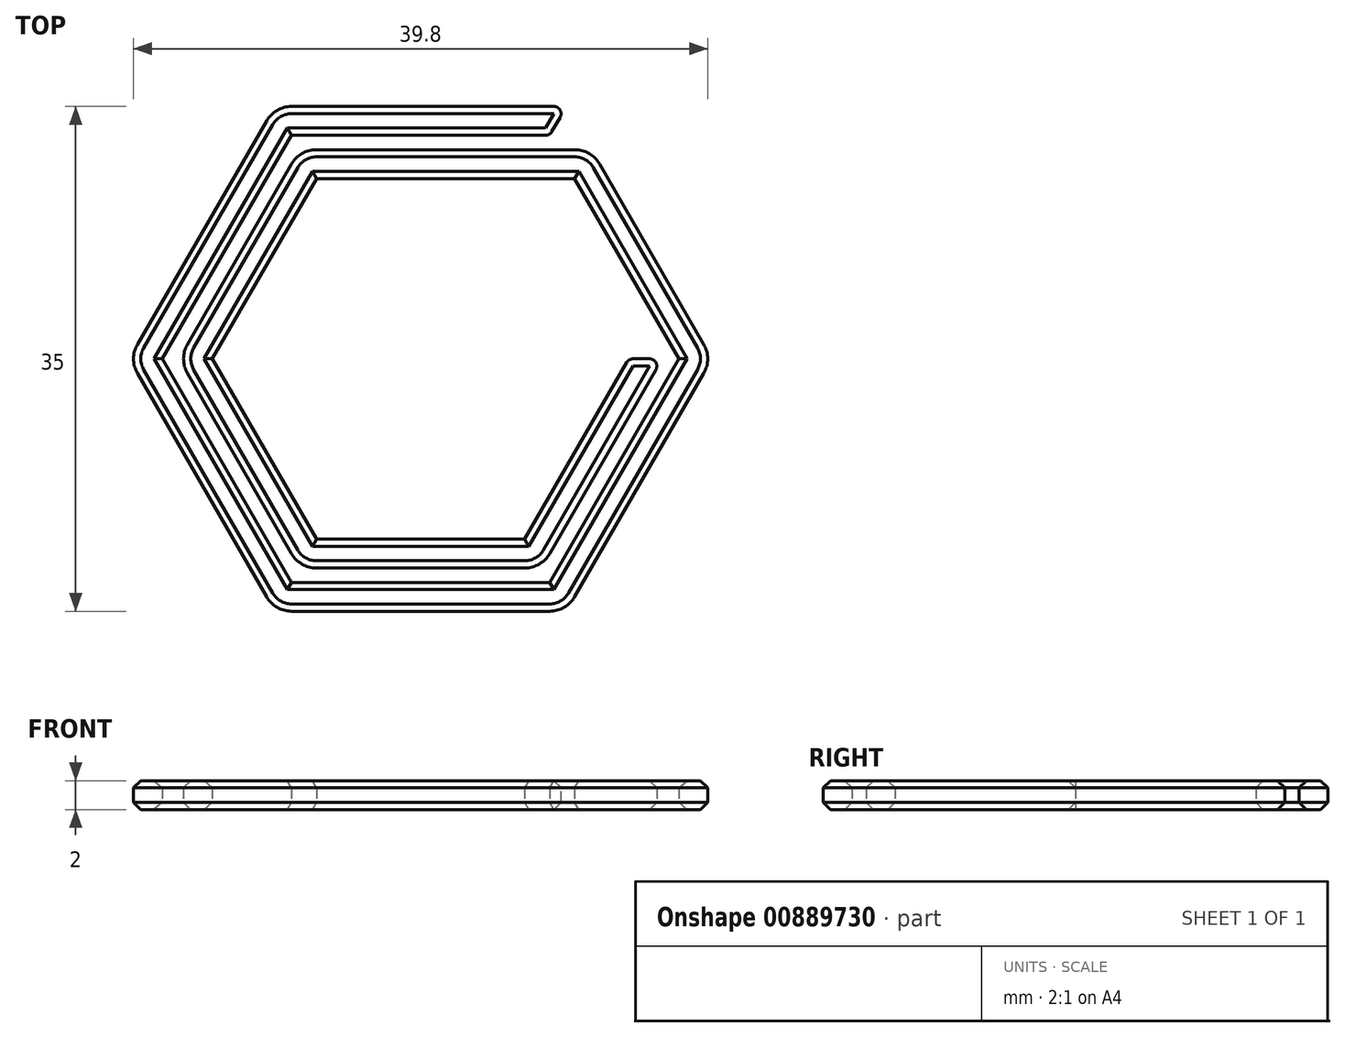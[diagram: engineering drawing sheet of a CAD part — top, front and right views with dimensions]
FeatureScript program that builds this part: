
annotation { "Feature Type Name" : "Feature", "Feature Type Description" : "" }
export const myFeature = defineFeature(function(context is Context, id is Id, definition is map)
    precondition{}
    {
        {
            var Q0;
            Q0=qCreatedBy(makeId("Top.planeOp"),FACE);
            var sketch = newSketch(context, id + "F0", { "sketchPlane" : qUnion([Q0])});
            skCircle(sketch, "E0.cCircle", {"center": v(0, 0) * mm, "radius": 12.5 * mm, "construction": true});
            skLineSegment(sketch, "E0.0", {"start": v(-7.22, 12.5) * mm, "end": v(7.22, 12.5) * mm});
            skLineSegment(sketch, "E0.2", {"start": v(14.43, 0) * mm, "end": v(7.22, -12.5) * mm});
            skLineSegment(sketch, "E0.3", {"start": v(7.22, -12.5) * mm, "end": v(-7.22, -12.5) * mm});
            skLineSegment(sketch, "E0.4", {"start": v(-7.22, -12.5) * mm, "end": v(-14.43, 0) * mm});
            skLineSegment(sketch, "E0.5", {"start": v(-14.43, 0) * mm, "end": v(-7.22, 12.5) * mm});
            skPoint(sketch, "E0.0.midPoint", {"position": v(0, 12.5) * mm});
            skLineSegment(sketch, "E1.0", {"start": v(-8.37, -14.5) * mm, "end": v(-16.74, 0) * mm});
            skLineSegment(sketch, "E1.1", {"start": v(-8.37, 14.5) * mm, "end": v(8.37, 14.5) * mm});
            skLineSegment(sketch, "E1.3", {"start": v(-16.74, 0) * mm, "end": v(-8.37, 14.5) * mm});
            skLineSegment(sketch, "E1.4", {"start": v(16.74, 0) * mm, "end": v(8.37, -14.5) * mm});
            skLineSegment(sketch, "E1.5", {"start": v(8.37, -14.5) * mm, "end": v(-8.37, -14.5) * mm});
            skLineSegment(sketch, "E2.0", {"start": v(-8.95, -15.5) * mm, "end": v(-17.9, 0) * mm});
            skLineSegment(sketch, "E2.1", {"start": v(-8.95, 15.5) * mm, "end": v(8.95, 15.5) * mm});
            skLineSegment(sketch, "E2.2", {"start": v(10.68, 12.5) * mm, "end": v(17.9, 0) * mm});
            skLineSegment(sketch, "E2.3", {"start": v(-17.9, 0) * mm, "end": v(-8.95, 15.5) * mm});
            skLineSegment(sketch, "E2.4", {"start": v(17.9, 0) * mm, "end": v(8.95, -15.5) * mm});
            skLineSegment(sketch, "E2.5", {"start": v(8.95, -15.5) * mm, "end": v(-8.95, -15.5) * mm});
            skLineSegment(sketch, "E3.0", {"start": v(-20.2, 0) * mm, "end": v(-10.1, 17.5) * mm});
            skLineSegment(sketch, "E3.1", {"start": v(11.84, 14.5) * mm, "end": v(20.2, 0) * mm});
            skLineSegment(sketch, "E3.2", {"start": v(20.2, 0) * mm, "end": v(10.1, -17.5) * mm});
            skLineSegment(sketch, "E3.3", {"start": v(-10.1, 17.5) * mm, "end": v(10.1, 17.5) * mm});
            skLineSegment(sketch, "E3.4", {"start": v(10.1, -17.5) * mm, "end": v(-10.1, -17.5) * mm});
            skLineSegment(sketch, "E3.5", {"start": v(-10.1, -17.5) * mm, "end": v(-20.2, 0) * mm});
            skLineSegment(sketch, "E4", {"start": v(8.37, 14.5) * mm, "end": v(11.84, 14.5) * mm});
            skLineSegment(sketch, "E5", {"start": v(9.53, 12.5) * mm, "end": v(10.68, 12.5) * mm});
            skLineSegment(sketch, "E6", {"start": v(8.95, 15.5) * mm, "end": v(10.1, 17.5) * mm});
            skLineSegment(sketch, "E7", {"start": v(7.22, 12.5) * mm, "end": v(9.53, 12.5) * mm});
            skLineSegment(sketch, "E8", {"start": v(14.43, 0) * mm, "end": v(16.74, 0) * mm});
            skSolve(sketch);
        }
        {
            var Q0;
            Q0=makeQuery(id+"F0.imprint","IMPRINT",FACE,{"disambiguationData":[TD([[makeQuery(id+"F0.imprint","IMPRINT",EDGE,{"derivedFrom":sQuery(id+"F0.wireOp",EDGE,"E0.0")}),1.0]])]});
            extrude(context, id + "F1", {"entities" : qUnion([Q0]), "depth" : 2 * mm, "offsetDistance" : 25 * mm});
        }
        {
            var Q0;
            Q0=makeQuery(id+"F1.opExtrude","SWEPT_EDGE",EDGE,{"disambiguationData":[OSD([sQuery(id+"F0.wireOp",EDGE,"E1.4"),sQuery(id+"F0.wireOp",EDGE,"E8")])]});
            var Q1;
            Q1=makeQuery(id+"F1.opExtrude","SWEPT_EDGE",EDGE,{"disambiguationData":[OSD([sQuery(id+"F0.wireOp",EDGE,"E0.2"),sQuery(id+"F0.wireOp",EDGE,"E8")])]});
            var Q2;
            Q2=makeQuery(id+"F1.opExtrude","SWEPT_EDGE",EDGE,{"disambiguationData":[OSD([sQuery(id+"F0.wireOp",EDGE,"E3.3"),sQuery(id+"F0.wireOp",EDGE,"E6")])]});
            var Q3;
            Q3=makeQuery(id+"F1.opExtrude","SWEPT_EDGE",EDGE,{"disambiguationData":[OSD([sQuery(id+"F0.wireOp",EDGE,"E2.1"),sQuery(id+"F0.wireOp",EDGE,"E6")])]});
            fillet(context, id + "F2", {"entities" : qUnion([Q0, Q1, Q2, Q3]), "radius" : 0.5 * mm, "tangentPropagation" : true, "allowEdgeOverflow" : false});
        }
        {
            var Q0;
            Q0=makeQuery(id+"F1.opExtrude","SWEPT_EDGE",EDGE,{"disambiguationData":[OSD([sQuery(id+"F0.wireOp",EDGE,"E3.0"),sQuery(id+"F0.wireOp",EDGE,"E3.3")])]});
            var Q1;
            Q1=makeQuery(id+"F1.opExtrude","SWEPT_EDGE",EDGE,{"disambiguationData":[OSD([sQuery(id+"F0.wireOp",EDGE,"E3.0"),sQuery(id+"F0.wireOp",EDGE,"E3.5")])]});
            var Q2;
            Q2=makeQuery(id+"F1.opExtrude","SWEPT_EDGE",EDGE,{"disambiguationData":[OSD([sQuery(id+"F0.wireOp",EDGE,"E3.4"),sQuery(id+"F0.wireOp",EDGE,"E3.5")])]});
            var Q3;
            Q3=makeQuery(id+"F1.opExtrude","SWEPT_EDGE",EDGE,{"disambiguationData":[OSD([sQuery(id+"F0.wireOp",EDGE,"E3.2"),sQuery(id+"F0.wireOp",EDGE,"E3.4")])]});
            var Q4;
            Q4=makeQuery(id+"F1.opExtrude","SWEPT_EDGE",EDGE,{"disambiguationData":[OSD([sQuery(id+"F0.wireOp",EDGE,"E3.1"),sQuery(id+"F0.wireOp",EDGE,"E3.2")])]});
            var Q5;
            Q5=makeQuery(id+"F1.opExtrude","SWEPT_EDGE",EDGE,{"disambiguationData":[OSD([sQuery(id+"F0.wireOp",EDGE,"E3.1"),sQuery(id+"F0.wireOp",EDGE,"E4")])]});
            var Q6;
            Q6=makeQuery(id+"F1.opExtrude","SWEPT_EDGE",EDGE,{"disambiguationData":[OSD([sQuery(id+"F0.wireOp",EDGE,"E1.1"),sQuery(id+"F0.wireOp",EDGE,"E1.3")])]});
            var Q7;
            Q7=makeQuery(id+"F1.opExtrude","SWEPT_EDGE",EDGE,{"disambiguationData":[OSD([sQuery(id+"F0.wireOp",EDGE,"E1.0"),sQuery(id+"F0.wireOp",EDGE,"E1.3")])]});
            var Q8;
            Q8=makeQuery(id+"F1.opExtrude","SWEPT_EDGE",EDGE,{"disambiguationData":[OSD([sQuery(id+"F0.wireOp",EDGE,"E1.0"),sQuery(id+"F0.wireOp",EDGE,"E1.5")])]});
            var Q9;
            Q9=makeQuery(id+"F1.opExtrude","SWEPT_EDGE",EDGE,{"disambiguationData":[OSD([sQuery(id+"F0.wireOp",EDGE,"E1.4"),sQuery(id+"F0.wireOp",EDGE,"E1.5")])]});
            fillet(context, id + "F3", {"entities" : qUnion([Q0, Q1, Q2, Q3, Q4, Q5, Q6, Q7, Q8, Q9]), "radius" : 2 * mm, "tangentPropagation" : true, "allowEdgeOverflow" : false});
        }
        {
            var Q0;
            Q0=makeQuery(id+"F1.opExtrude","CAP_FACE",FACE,{"disambiguationData":[OSD([sQuery(id+"F0.wireOp",EDGE,"E0.0"),sQuery(id+"F0.wireOp",EDGE,"E0.2"),sQuery(id+"F0.wireOp",EDGE,"E0.3"),sQuery(id+"F0.wireOp",EDGE,"E0.4"),sQuery(id+"F0.wireOp",EDGE,"E0.5"),sQuery(id+"F0.wireOp",EDGE,"E1.0"),sQuery(id+"F0.wireOp",EDGE,"E1.1"),sQuery(id+"F0.wireOp",EDGE,"E1.3"),sQuery(id+"F0.wireOp",EDGE,"E1.4"),sQuery(id+"F0.wireOp",EDGE,"E1.5"),sQuery(id+"F0.wireOp",EDGE,"E2.0"),sQuery(id+"F0.wireOp",EDGE,"E2.1"),sQuery(id+"F0.wireOp",EDGE,"E2.2"),sQuery(id+"F0.wireOp",EDGE,"E2.3"),sQuery(id+"F0.wireOp",EDGE,"E2.4"),sQuery(id+"F0.wireOp",EDGE,"E2.5"),sQuery(id+"F0.wireOp",EDGE,"E3.0"),sQuery(id+"F0.wireOp",EDGE,"E3.1"),sQuery(id+"F0.wireOp",EDGE,"E3.2"),sQuery(id+"F0.wireOp",EDGE,"E3.3"),sQuery(id+"F0.wireOp",EDGE,"E3.4"),sQuery(id+"F0.wireOp",EDGE,"E3.5"),sQuery(id+"F0.wireOp",EDGE,"E4"),sQuery(id+"F0.wireOp",EDGE,"E5"),sQuery(id+"F0.wireOp",EDGE,"E6"),sQuery(id+"F0.wireOp",EDGE,"E7"),sQuery(id+"F0.wireOp",EDGE,"E8")])],"isStart":true});
            var Q1;
            Q1=makeQuery(id+"F1.opExtrude","CAP_FACE",FACE,{"disambiguationData":[OSD([sQuery(id+"F0.wireOp",EDGE,"E0.0"),sQuery(id+"F0.wireOp",EDGE,"E0.2"),sQuery(id+"F0.wireOp",EDGE,"E0.3"),sQuery(id+"F0.wireOp",EDGE,"E0.4"),sQuery(id+"F0.wireOp",EDGE,"E0.5"),sQuery(id+"F0.wireOp",EDGE,"E1.0"),sQuery(id+"F0.wireOp",EDGE,"E1.1"),sQuery(id+"F0.wireOp",EDGE,"E1.3"),sQuery(id+"F0.wireOp",EDGE,"E1.4"),sQuery(id+"F0.wireOp",EDGE,"E1.5"),sQuery(id+"F0.wireOp",EDGE,"E2.0"),sQuery(id+"F0.wireOp",EDGE,"E2.1"),sQuery(id+"F0.wireOp",EDGE,"E2.2"),sQuery(id+"F0.wireOp",EDGE,"E2.3"),sQuery(id+"F0.wireOp",EDGE,"E2.4"),sQuery(id+"F0.wireOp",EDGE,"E2.5"),sQuery(id+"F0.wireOp",EDGE,"E3.0"),sQuery(id+"F0.wireOp",EDGE,"E3.1"),sQuery(id+"F0.wireOp",EDGE,"E3.2"),sQuery(id+"F0.wireOp",EDGE,"E3.3"),sQuery(id+"F0.wireOp",EDGE,"E3.4"),sQuery(id+"F0.wireOp",EDGE,"E3.5"),sQuery(id+"F0.wireOp",EDGE,"E4"),sQuery(id+"F0.wireOp",EDGE,"E5"),sQuery(id+"F0.wireOp",EDGE,"E6"),sQuery(id+"F0.wireOp",EDGE,"E7"),sQuery(id+"F0.wireOp",EDGE,"E8")])],"isStart":false});
            chamfer(context, id + "F4", {"entities" : qUnion([Q0, Q1]), "width" : 0.5 * mm, "tangentPropagation" : true});
        }
    });
